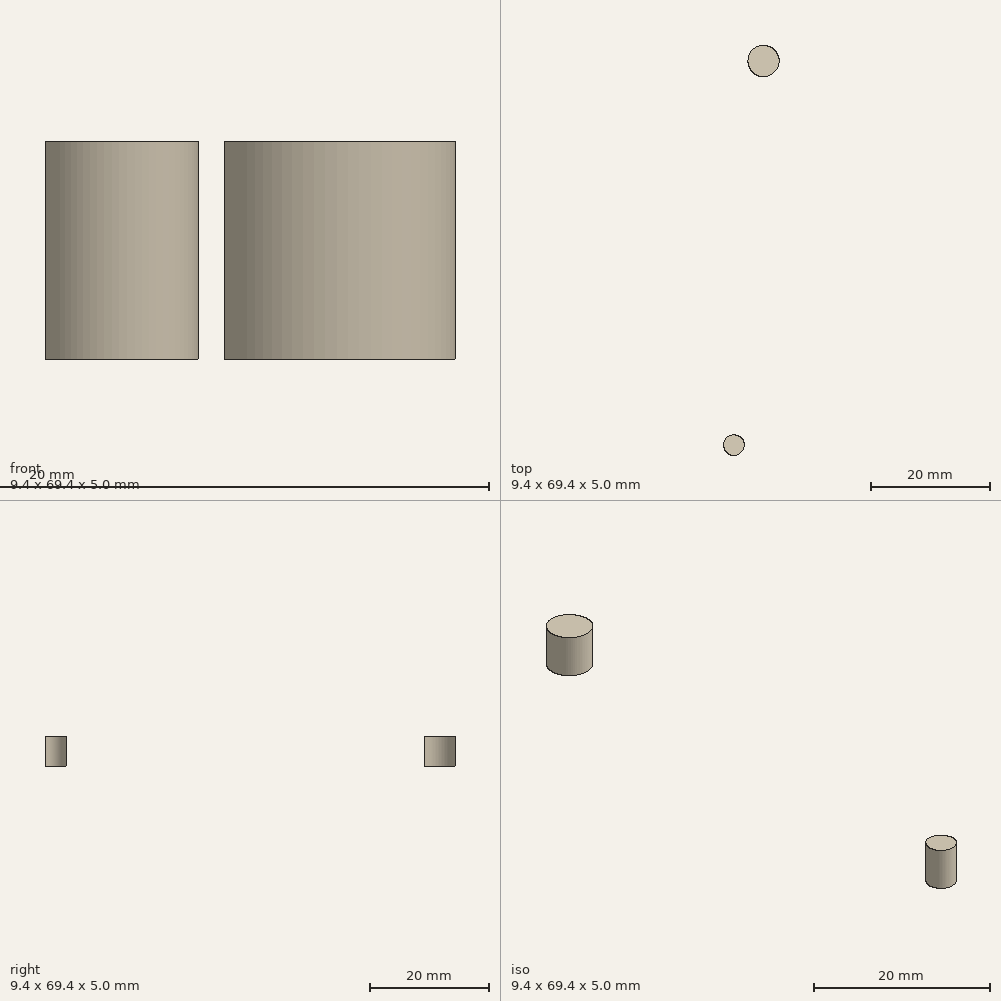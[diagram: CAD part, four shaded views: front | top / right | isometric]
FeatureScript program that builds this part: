
annotation { "Feature Type Name" : "Feature", "Feature Type Description" : "" }
export const myFeature = defineFeature(function(context is Context, id is Id, definition is map)
    precondition{}
    {
        {
            var Q0;
            Q0=qCreatedBy(makeId("Top.planeOp"),FACE);
            var sketch = newSketch(context, id + "F0", { "sketchPlane" : qUnion([Q0])});
            skLineSegment(sketch, "E0.bottom", {"start": v(-34.85, 74.64) * mm, "end": v(45.15, 74.64) * mm});
            skLineSegment(sketch, "E0.top", {"start": v(-34.85, -25.36) * mm, "end": v(45.15, -25.36) * mm});
            skLineSegment(sketch, "E0.left", {"start": v(-34.85, 74.64) * mm, "end": v(-34.85, -25.36) * mm});
            skLineSegment(sketch, "E0.right", {"start": v(45.15, 74.64) * mm, "end": v(45.15, -25.36) * mm});
            skSolve(sketch);
        }
        {
            var Q0;
            Q0=makeQuery(id+"F0.imprint","IMPRINT",FACE,{"disambiguationData":[TD([[makeQuery(id+"F0.imprint","IMPRINT",EDGE,{"derivedFrom":sQuery(id+"F0.wireOp",EDGE,"E0.bottom")}),-1.0]])]});
            var Q1;
            Q1=sQuery(id+"F0.wireOp",EDGE,"E0.right");
            var Q2;
            Q2=sQuery(id+"F0.wireOp",EDGE,"E0.left");
            var Q3;
            Q3=sQuery(id+"F0.wireOp",EDGE,"E0.top");
            var Q4;
            Q4=sQuery(id+"F0.wireOp",EDGE,"E0.bottom");
            extrude(context, id + "F1", {"entities" : qUnion([Q0]), "surfaceEntities" : qUnion([Q1, Q2, Q3, Q4]), "depth" : 5 * mm});
        }
        {
            var Q0;
            Q0=makeQuery(id+"F1.opExtrude","CAP_FACE",FACE,{"disambiguationData":[OSD([sQuery(id+"F0.wireOp",EDGE,"E0.bottom"),sQuery(id+"F0.wireOp",EDGE,"E0.top"),sQuery(id+"F0.wireOp",EDGE,"E0.left"),sQuery(id+"F0.wireOp",EDGE,"E0.right")])],"isStart":false});
            var sketch = newSketch(context, id + "F2", { "sketchPlane" : qUnion([Q0])});
            skLineSegment(sketch, "E1", {"start": v(-34.85, 49.64) * mm, "end": v(45.15, 49.64) * mm, "construction": true});
            skLineSegment(sketch, "E2", {"start": v(5.15, -25.36) * mm, "end": v(5.15, 74.64) * mm, "construction": true});
            skLineSegment(sketch, "E3", {"start": v(-34.85, -15.36) * mm, "end": v(45.15, -15.36) * mm, "construction": true});
            skCircle(sketch, "E4", {"center": v(-24.85, 49.64) * mm, "radius": 2.65 * mm});
            skCircle(sketch, "E5", {"center": v(-19.85, -15.36) * mm, "radius": 1.75 * mm});
            skCircle(sketch, "E6.MirrorC", {"center": v(35.15, 49.64) * mm, "radius": 2.65 * mm});
            skCircle(sketch, "E7.MirrorC", {"center": v(30.15, -15.36) * mm, "radius": 1.75 * mm});
            skSolve(sketch);
        }
        {
            var Q0;
            Q0=makeQuery(id+"F2.imprint","IMPRINT",FACE,{"disambiguationData":[TD([[makeQuery(id+"F2.imprint","IMPRINT",EDGE,{"derivedFrom":sQuery(id+"F2.wireOp",EDGE,"E5")}),1.0]])]});
            var Q1;
            Q1=makeQuery(id+"F2.imprint","IMPRINT",FACE,{"disambiguationData":[TD([[makeQuery(id+"F2.imprint","IMPRINT",EDGE,{"derivedFrom":sQuery(id+"F2.wireOp",EDGE,"E6.MirrorC")}),-1.0]])]});
            var Q2;
            Q2=makeQuery(id+"F2.imprint","IMPRINT",FACE,{"disambiguationData":[TD([[makeQuery(id+"F2.imprint","IMPRINT",EDGE,{"derivedFrom":sQuery(id+"F2.wireOp",EDGE,"E4")}),1.0]])]});
            var Q3;
            Q3=makeQuery(id+"F2.imprint","IMPRINT",FACE,{"disambiguationData":[TD([[makeQuery(id+"F2.imprint","IMPRINT",EDGE,{"derivedFrom":sQuery(id+"F2.wireOp",EDGE,"E7.MirrorC")}),-1.0]])]});
            var Q4;
            Q4=makeQuery(id+"F1.opExtrude","CAP_FACE",FACE,{"disambiguationData":[OSD([sQuery(id+"F0.wireOp",EDGE,"E0.bottom"),sQuery(id+"F0.wireOp",EDGE,"E0.top"),sQuery(id+"F0.wireOp",EDGE,"E0.left"),sQuery(id+"F0.wireOp",EDGE,"E0.right")])],"isStart":true});
            extrude(context, id + "F3", {"entities" : qUnion([Q0, Q1, Q2, Q3]), "operationType" : NewBodyOperationType.REMOVE, "endBound" : BoundingType.UP_TO_SURFACE, "oppositeDirection" : true, "endBoundEntityFace" : qUnion([Q4]), "depth" : 25 * mm});
        }
    });
